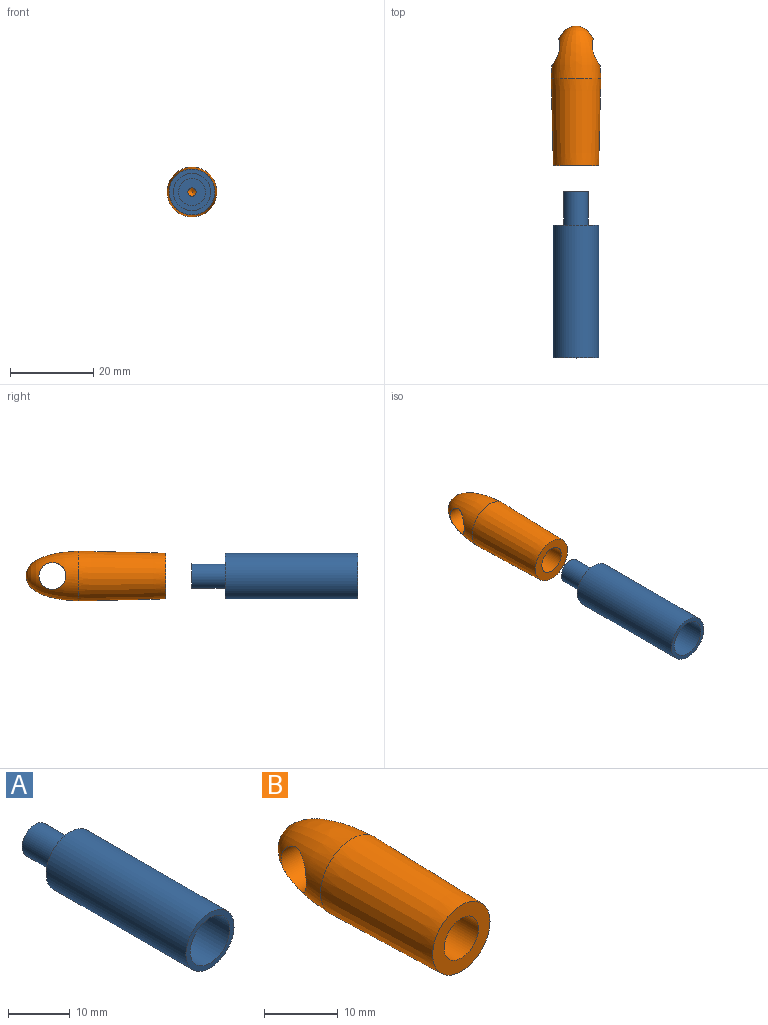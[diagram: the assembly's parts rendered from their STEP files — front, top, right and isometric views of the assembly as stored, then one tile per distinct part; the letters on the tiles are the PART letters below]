
ASSEMBLY  parts=2 mates=1
PART A: 10 faces, bbox 11x40x11 mm
  f0: plane 11x11mm, normal (0,-1,0), area 31.4mm2, adj f1,f9
  f1: cylinder r=4.5mm len=10mm, axis (0,1,0), area 282.7mm2, adj f0,f2
  f2: plane 9x9mm, normal (0,-1,0), area 30.4mm2, adj f1,f3
  f3: cylinder r=3.25mm len=20mm, axis (0,1,0), area 408.4mm2, adj f2,f4
  f4: plane 6.5x6.5mm, normal (0,-1,0), area 30mm2, adj f3,f5
  f5: cylinder r=1mm len=10mm, axis (0,1,0), area 62.8mm2, adj f4,f6
  f6: plane 6x6mm, normal (0,1,0), area 25.1mm2, adj f5,f7
  f7: cylinder r=3mm len=8mm, axis (0,1,0), area 150.8mm2, adj f6,f8
  f8: plane 11x11mm, normal (0,1,0), area 66.8mm2, adj f7,f9
  f9: cylinder r=5.5mm len=32mm, axis (0,1,0), area 1105.8mm2, adj f0,f8
PART B: 6 faces, bbox 12x33.6x12 mm
  f0: revolved ~12.59x12mm, area 335.4mm2, adj f2,f3
  f1: cone r=5.5mm half-angle=89.9deg, axis (0,-1,0), area 60.8mm2, adj f2,f5
  f2: cone r=5.5mm half-angle=1.4deg, axis (0,1,0), area 758.9mm2, adj f0,f1
  f3: cylinder r=3.25mm len=11.58mm, axis (1,0,0), area 186.6mm2, adj f0
  f4: cone r=0mm half-angle=59deg, axis (0,-1,0), area 39.9mm2, adj f5
  f5: cylinder r=3.3mm len=15mm, axis (0,-1,0), area 311mm2, adj f1,f4
PLACE A rot(axis=(0,1,0),180deg) t=(3.18,-42.39,6.63)mm
PLACE B t=(3.18,3.94,6.63)mm
MATE slider B.f1 <-> A.f1  axis (0,-1,0) through (3.18,3.94,6.63)mm
